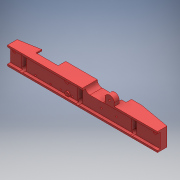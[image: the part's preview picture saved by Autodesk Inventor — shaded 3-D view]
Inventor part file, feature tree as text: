
AUTODESK INVENTOR PART (.ipt)
format: ipt  version: 2017 (Build 210142000, 142)  size: 727,552 bytes
history: native  units: mm
features: reference x27, projected_geometry x13, sketch x11, extrude x10, other x7, fillet x4, hole x3, plane x1
ambient origin geometry x8: Origin, YZ Plane, XZ Plane, XY Plane, X Axis, Y Axis, Z Axis, Center Point
bodies: Solid1 (feature_tree)
feature tree (76):
  extrude  "Extrusion1"  TaperAngle=0.0deg  [1 undecoded]
  extrude  "Extrusion2"  Depth=17.453293mm
  extrude  "Extrusion3"  Depth=8.0mm
  extrude  "Extrusion4"  Depth=3.0mm TaperAngle=0.0deg
  extrude  "Extrusion5"  Depth=4.0mm
  fillet  "Fillet1"  Radius=4.0mm
  sketch  "Sketch6"  dims[d13=1.8mm d14=1.2mm d15=0.0mm]
  plane  "Work Plane1"
  extrude  "Extrusion6"  Depth=1.8mm TaperAngle=0.0deg
  extrude  "Extrusion7"  Depth=1.5mm TaperAngle=0.0deg
  hole  "Hole1"  [1 undecoded]
  hole  "Hole2"  [1 undecoded]
  extrude  "Extrusion8"  Depth=3.0mm
  extrude  "Extrusion9"  Depth=8.0mm TaperAngle=0.0deg
  extrude  "Extrusion10"  Depth=8.0mm TaperAngle=0.0deg
  fillet  "Fillet2"  Radius=10.0mm
  fillet  "Fillet3"  Radius=1.6mm
  fillet  "Fillet4"  Radius=1.6mm
  hole  "Hole3"  [1 undecoded]
  sketch  "Sketch1"  dims[d0=17.453293mm d1=0.0mm]
  reference  "Reference1"
  reference  "Reference2"
  reference  "Reference3"
  reference  "Reference4"
  reference  "Reference5"
  reference  "Reference6"
  sketch  "Sketch2"  dims[d2=0.0mm d3=17.453293mm]
  projected_geometry  "Projected Loop1"
  sketch  "Sketch3"  dims[d4=20.0mm d5=0.0mm d6=8.0mm]
  projected_geometry  "Projected Loop2"
  sketch  "Sketch4"  dims[d7=16.0mm d8=3.0mm d9=0.0mm]
  projected_geometry  "Projected Loop3"
  reference  "Reference7"
  reference  "Reference8"
  reference  "Reference9"
  reference  "Reference10"
  reference  "Reference11"
  reference  "Reference12"
  reference  "Reference13"
  sketch  "Sketch5"  dims[d10=4.0mm d11=154.0mm d12=4.0mm]
  projected_geometry  "Projected Loop4"
  projected_geometry  "Projected Loop5"
  reference  "Reference14"
  reference  "Reference15"
  sketch  "Sketch7"  dims[d16=5.0mm d17=1.5mm d18=0.0mm]
  projected_geometry  "Projected Loop6"
  reference  "Reference18"
  reference  "Reference19"
  reference  "Reference20"
  reference  "Reference21"
  reference  "Reference22"
  reference  "Reference23"
  reference  "Reference24"
  reference  "Reference25"
  sketch  "Sketch9"  dims[d19=5.0mm d20=5.0mm]
  reference  "Reference26"
  reference  "Reference27"
  reference  "Reference28"
  sketch  "Sketch10"  dims[d21=3.6mm d22=1.5mm d23=0.0mm]
  reference  "Reference29"
  sketch  "Sketch11"  dims[d24=3.0mm d25=5.0mm]
  projected_geometry  "Projected Loop7"
  sketch  "Sketch12"  dims[d26=5.0mm d27=1.5mm d28=0.0mm d29=5.25mm d30=0.0mm d31=10.0mm d32=1.4mm d33=6.0mm d34=4.0mm d35=2.0mm d36=90.0deg d37=8.0mm d38=20.594885mm d69=10.0mm d70=10.0mm d41=1.8mm d42=6.0mm d43=4.0mm d44=2.0mm d45=90.0deg d46=8.0mm d47=20.594885mm d48=1.6mm d49=1.6mm d50=2.0mm d51=0.0mm d52=2.0mm d53=0.0mm d54=10.0mm d55=4.0mm d56=0.0mm d57=4.0mm d58=4.0mm d59=2.0mm d60=1.4mm d61=6.0mm d62=4.0mm d63=2.0mm d64=90.0deg d65=8.0mm d66=20.594885mm d67=16.5mm d68=5.0mm]
  projected_geometry  "Projected Loop8"
  projected_geometry  "Projected Loop9"
  projected_geometry  "Projected Loop10"
  projected_geometry  "Projected Loop11"
  projected_geometry  "Projected Loop12"
  projected_geometry  "Projected Loop13"
  other  "<userpath>\Dropbox\Work\HeadSLAM\xtion_custom_assembly.iam"
  other  "xtion_custom_assembly.iam"
  other  "xtion_heatsink:1"
  other  "xtion_projector:1"
  other  "xtion_mainboard:1"
  other  "xtion_rgb_cam:1"
  other  "xtion_ir_cam:1"
note: 4 required parameter values undecoded (feature->parameter linkage not recoverable at this tier; creation-order binding heuristic only, values carry confidence <= 0.55)
